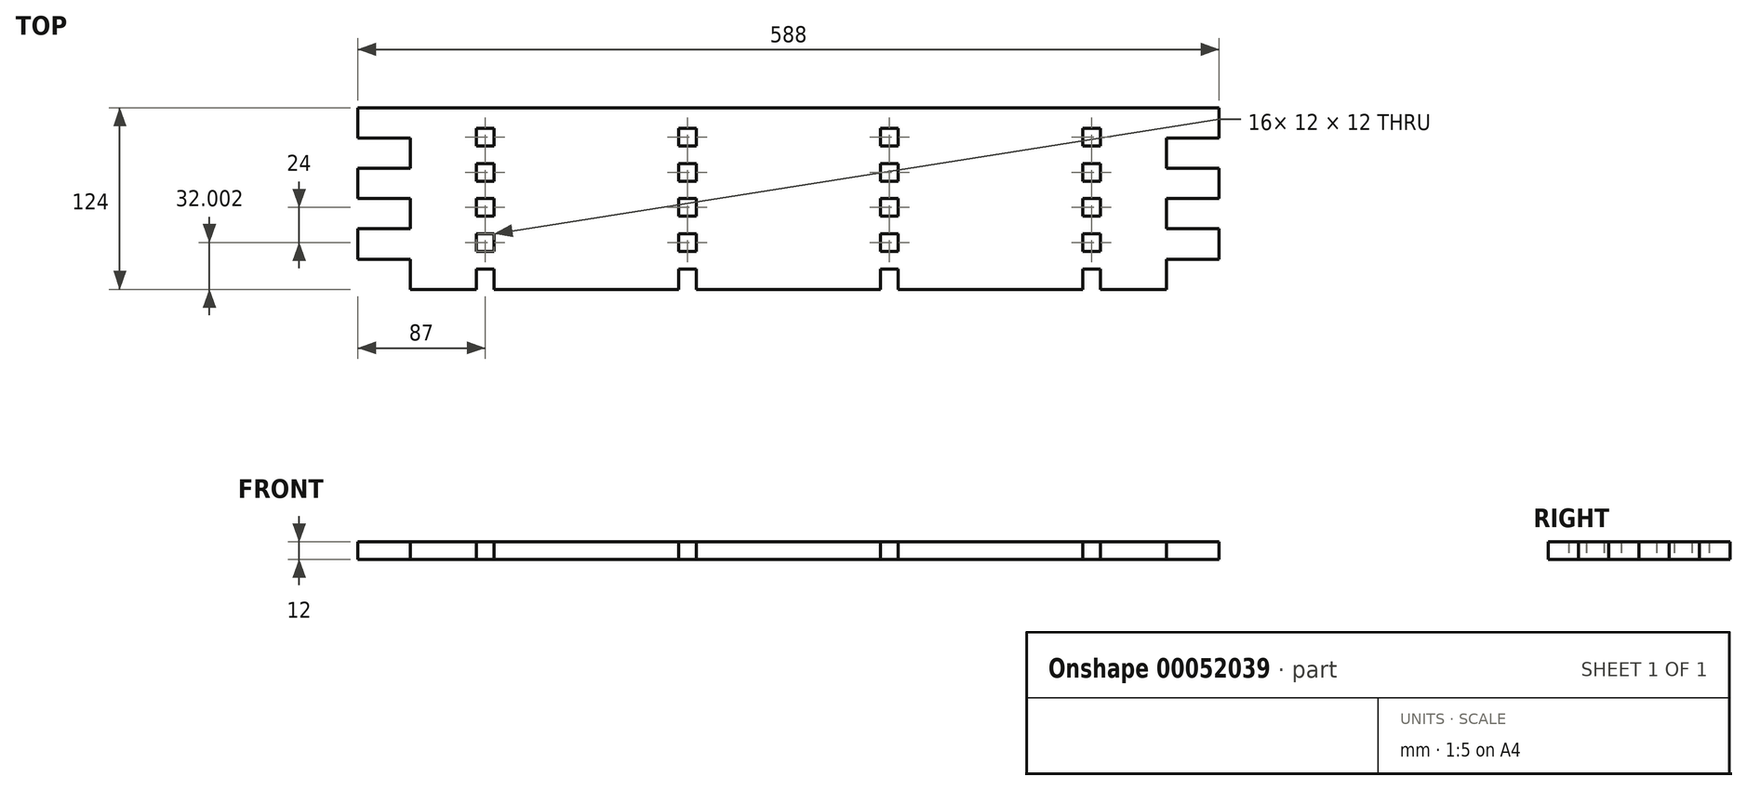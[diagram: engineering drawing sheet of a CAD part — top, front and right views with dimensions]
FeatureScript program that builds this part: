
annotation { "Feature Type Name" : "Feature", "Feature Type Description" : "" }
export const myFeature = defineFeature(function(context is Context, id is Id, definition is map)
    precondition{}
    {
        {
            var Q0;
            Q0=qCreatedBy(makeId("Top.planeOp"),FACE);
            var sketch = newSketch(context, id + "F0", { "sketchPlane" : qUnion([Q0])});
            skLineSegment(sketch, "E0.rect.bottom", {"start": v(489, 62) * mm, "end": v(-489, 62) * mm, "construction": true});
            skLineSegment(sketch, "E0.rect.top", {"start": v(489, -62) * mm, "end": v(-489, -62) * mm, "construction": true});
            skLineSegment(sketch, "E0.rect.left", {"start": v(489, 62) * mm, "end": v(489, -62) * mm, "construction": true});
            skLineSegment(sketch, "E0.rect.right", {"start": v(-489, 62) * mm, "end": v(-489, -62) * mm, "construction": true});
            skPoint(sketch, "E0.rect.middle", {"position": v(0, 0) * mm});
            skLineSegment(sketch, "E1", {"start": v(-489, 120.38) * mm, "end": v(-477, 120.38) * mm, "construction": true});
            skLineSegment(sketch, "E2", {"start": v(-477, 120.38) * mm, "end": v(-351, 120.38) * mm, "construction": true});
            skLineSegment(sketch, "E3.1.0.0", {"start": v(-351, 120.38) * mm, "end": v(-339, 120.38) * mm, "construction": true});
            skLineSegment(sketch, "E3.1.0.1", {"start": v(-339, 120.38) * mm, "end": v(-213, 120.38) * mm, "construction": true});
            skLineSegment(sketch, "E3.2.0.0", {"start": v(-213, 120.38) * mm, "end": v(-201, 120.38) * mm, "construction": true});
            skLineSegment(sketch, "E3.2.0.1", {"start": v(-201, 120.38) * mm, "end": v(-75, 120.38) * mm, "construction": true});
            skLineSegment(sketch, "E3.3.0.0", {"start": v(-75, 120.38) * mm, "end": v(-63, 120.38) * mm, "construction": true});
            skLineSegment(sketch, "E3.3.0.1", {"start": v(-63, 120.38) * mm, "end": v(63, 120.38) * mm, "construction": true});
            skLineSegment(sketch, "E3.4.0.0", {"start": v(63, 120.38) * mm, "end": v(75, 120.38) * mm, "construction": true});
            skLineSegment(sketch, "E3.4.0.1", {"start": v(75, 120.38) * mm, "end": v(201, 120.38) * mm, "construction": true});
            skLineSegment(sketch, "E3.5.0.0", {"start": v(201, 120.38) * mm, "end": v(213, 120.38) * mm, "construction": true});
            skLineSegment(sketch, "E3.5.0.1", {"start": v(213, 120.38) * mm, "end": v(339, 120.38) * mm, "construction": true});
            skLineSegment(sketch, "E3.6.0.0", {"start": v(339, 120.38) * mm, "end": v(351, 120.38) * mm, "construction": true});
            skLineSegment(sketch, "E3.6.0.1", {"start": v(351, 120.38) * mm, "end": v(477, 120.38) * mm, "construction": true});
            skLineSegment(sketch, "E3.direction1", {"start": v(-489, 120.38) * mm, "end": v(-351, 120.38) * mm, "construction": true});
            skLineSegment(sketch, "E4", {"start": v(477, 120.38) * mm, "end": v(489, 120.38) * mm, "construction": true});
            skLineSegment(sketch, "E5", {"start": v(-294, 207.07) * mm, "end": v(-213, 207.07) * mm, "construction": true});
            skPoint(sketch, "E6", {"position": v(0, 207.07) * mm});
            skLineSegment(sketch, "E7", {"start": v(258, 476.96) * mm, "end": v(489, 476.96) * mm, "construction": true});
            skLineSegment(sketch, "E8", {"start": v(294, 207.07) * mm, "end": v(294, 331.07) * mm, "construction": true});
            skLineSegment(sketch, "E9", {"start": v(294, 331.07) * mm, "end": v(-294, 331.07) * mm, "construction": true});
            skLineSegment(sketch, "E10", {"start": v(-294, 331.07) * mm, "end": v(-294, 207.07) * mm, "construction": true});
            skLineSegment(sketch, "E11", {"start": v(258, 289.74) * mm, "end": v(294, 289.74) * mm});
            skLineSegment(sketch, "E12", {"start": v(294, 289.74) * mm, "end": v(294, 269.07) * mm});
            skLineSegment(sketch, "E13", {"start": v(294, 269.07) * mm, "end": v(258, 269.07) * mm});
            skLineSegment(sketch, "E14", {"start": v(258, 269.07) * mm, "end": v(258, 248.4) * mm});
            skLineSegment(sketch, "E15", {"start": v(258, 248.4) * mm, "end": v(294, 248.4) * mm});
            skLineSegment(sketch, "E16", {"start": v(294, 248.4) * mm, "end": v(294, 227.74) * mm});
            skLineSegment(sketch, "E17", {"start": v(294, 227.74) * mm, "end": v(258, 227.74) * mm});
            skLineSegment(sketch, "E18", {"start": v(258, 227.74) * mm, "end": v(258, 207.07) * mm});
            skLineSegment(sketch, "E19", {"start": v(258, 289.74) * mm, "end": v(258, 310.4) * mm});
            skLineSegment(sketch, "E20", {"start": v(258, 310.4) * mm, "end": v(294, 310.4) * mm});
            skLineSegment(sketch, "E21", {"start": v(294, 310.4) * mm, "end": v(294, 331.07) * mm});
            skLineSegment(sketch, "E22", {"start": v(0, 207.07) * mm, "end": v(63, 207.07) * mm});
            skLineSegment(sketch, "E23", {"start": v(0, 331.07) * mm, "end": v(294, 331.07) * mm});
            skLineSegment(sketch, "E24", {"start": v(0, 331.07) * mm, "end": v(0, 207.07) * mm, "construction": true});
            skLineSegment(sketch, "E25.MirrorCS", {"start": v(0, 331.07) * mm, "end": v(-294, 331.07) * mm});
            skLineSegment(sketch, "E26.MirrorCS", {"start": v(0, 207.07) * mm, "end": v(-63, 207.07) * mm});
            skLineSegment(sketch, "E27.MirrorCS", {"start": v(-294, 227.74) * mm, "end": v(-258, 227.74) * mm});
            skLineSegment(sketch, "E28.MirrorCS", {"start": v(-258, 310.4) * mm, "end": v(-294, 310.4) * mm});
            skLineSegment(sketch, "E29.MirrorCS", {"start": v(-294, 269.07) * mm, "end": v(-258, 269.07) * mm});
            skLineSegment(sketch, "E30.MirrorCS", {"start": v(-258, 289.74) * mm, "end": v(-294, 289.74) * mm});
            skLineSegment(sketch, "E31.MirrorCS", {"start": v(-258, 248.4) * mm, "end": v(-294, 248.4) * mm});
            skLineSegment(sketch, "E32.MirrorCS", {"start": v(-258, 227.74) * mm, "end": v(-258, 207.07) * mm});
            skLineSegment(sketch, "E33.MirrorCS", {"start": v(-258, 269.07) * mm, "end": v(-258, 248.4) * mm});
            skLineSegment(sketch, "E34.MirrorCS", {"start": v(-258, 289.74) * mm, "end": v(-258, 310.4) * mm});
            skLineSegment(sketch, "E35.MirrorCS", {"start": v(-294, 207.07) * mm, "end": v(-294, 331.07) * mm, "construction": true});
            skLineSegment(sketch, "E36", {"start": v(-294, 331.07) * mm, "end": v(-294, 310.4) * mm});
            skLineSegment(sketch, "E37", {"start": v(-294, 289.74) * mm, "end": v(-294, 269.07) * mm});
            skLineSegment(sketch, "E38", {"start": v(-294, 227.74) * mm, "end": v(-294, 248.4) * mm, "construction": true});
            skLineSegment(sketch, "E39", {"start": v(-294, 227.74) * mm, "end": v(-294, 248.4) * mm});
            skPoint(sketch, "E40", {"position": v(276, 227.74) * mm});
            skPoint(sketch, "E41", {"position": v(276, 120.38) * mm});
            skLineSegment(sketch, "E42", {"start": v(-213, 207.07) * mm, "end": v(-213, 331.07) * mm, "construction": true});
            skLineSegment(sketch, "E43", {"start": v(-201, 331.07) * mm, "end": v(-201, 207.07) * mm, "construction": true});
            skLineSegment(sketch, "E44", {"start": v(-213, 207.07) * mm, "end": v(-213, 221.07) * mm});
            skLineSegment(sketch, "E45", {"start": v(-213, 221.07) * mm, "end": v(-201, 221.07) * mm});
            skLineSegment(sketch, "E46", {"start": v(-201, 221.07) * mm, "end": v(-201, 207.07) * mm});
            skLineSegment(sketch, "E47", {"start": v(-213, 233.07) * mm, "end": v(-201, 233.07) * mm});
            skLineSegment(sketch, "E48", {"start": v(-201, 233.07) * mm, "end": v(-201, 245.07) * mm});
            skLineSegment(sketch, "E49", {"start": v(-201, 245.07) * mm, "end": v(-213, 245.07) * mm});
            skLineSegment(sketch, "E50", {"start": v(-213, 245.07) * mm, "end": v(-213, 233.07) * mm});
            skLineSegment(sketch, "E51", {"start": v(-294, 269.07) * mm, "end": v(0, 269.07) * mm, "construction": true});
            skLineSegment(sketch, "E52", {"start": v(-213, 257.07) * mm, "end": v(-213, 269.07) * mm});
            skLineSegment(sketch, "E53", {"start": v(-213, 269.07) * mm, "end": v(-201, 269.07) * mm});
            skLineSegment(sketch, "E54", {"start": v(-201, 269.07) * mm, "end": v(-201, 257.07) * mm});
            skLineSegment(sketch, "E55", {"start": v(-213, 257.07) * mm, "end": v(-201, 257.07) * mm});
            skLineSegment(sketch, "E56.trimOffspring", {"start": v(-201, 207.07) * mm, "end": v(-75, 207.07) * mm, "construction": true});
            skLineSegment(sketch, "E57.trimOffspring", {"start": v(-213, 207.07) * mm, "end": v(-258, 207.07) * mm});
            skLineSegment(sketch, "E58", {"start": v(-213, 269.07) * mm, "end": v(-213, 281.07) * mm, "construction": true});
            skLineSegment(sketch, "E59", {"start": v(-213, 281.07) * mm, "end": v(-213, 293.07) * mm, "construction": true});
            skLineSegment(sketch, "E60", {"start": v(-213, 293.07) * mm, "end": v(-213, 305.07) * mm, "construction": true});
            skLineSegment(sketch, "E61", {"start": v(-213, 305.07) * mm, "end": v(-213, 317.07) * mm, "construction": true});
            skLineSegment(sketch, "E62", {"start": v(-213, 281.07) * mm, "end": v(-201, 281.07) * mm});
            skLineSegment(sketch, "E63", {"start": v(-213, 293.07) * mm, "end": v(-201, 293.07) * mm});
            skLineSegment(sketch, "E64", {"start": v(-213, 317.07) * mm, "end": v(-201, 317.07) * mm});
            skLineSegment(sketch, "E65", {"start": v(-213, 305.07) * mm, "end": v(-201, 305.07) * mm});
            skLineSegment(sketch, "E66", {"start": v(-213, 293.07) * mm, "end": v(-213, 281.07) * mm});
            skLineSegment(sketch, "E67", {"start": v(-201, 293.07) * mm, "end": v(-201, 281.07) * mm});
            skLineSegment(sketch, "E68", {"start": v(-201, 305.07) * mm, "end": v(-201, 317.07) * mm});
            skLineSegment(sketch, "E69", {"start": v(-213, 317.07) * mm, "end": v(-213, 305.07) * mm});
            skLineSegment(sketch, "E70", {"start": v(-213, 207.07) * mm, "end": v(-201, 207.07) * mm, "construction": true});
            skLineSegment(sketch, "E71.1.0.0", {"start": v(-163, 221.07) * mm, "end": v(-151, 221.07) * mm});
            skLineSegment(sketch, "E71.2.0.0", {"start": v(-113, 221.07) * mm, "end": v(-101, 221.07) * mm});
            skLineSegment(sketch, "E71.direction1", {"start": v(-213, 221.07) * mm, "end": v(-163, 221.07) * mm, "construction": true});
            skLineSegment(sketch, "E72.1.0.0", {"start": v(-75, 269.07) * mm, "end": v(-63, 269.07) * mm});
            skLineSegment(sketch, "E72.1.0.1", {"start": v(-63, 221.07) * mm, "end": v(-63, 207.07) * mm});
            skLineSegment(sketch, "E72.1.0.2", {"start": v(-75, 269.07) * mm, "end": v(-75, 281.07) * mm, "construction": true});
            skLineSegment(sketch, "E72.1.0.3", {"start": v(-75, 293.07) * mm, "end": v(-75, 305.07) * mm, "construction": true});
            skLineSegment(sketch, "E72.1.0.4", {"start": v(-75, 293.07) * mm, "end": v(-63, 293.07) * mm});
            skLineSegment(sketch, "E72.1.0.5", {"start": v(-63, 305.07) * mm, "end": v(-63, 317.07) * mm});
            skLineSegment(sketch, "E72.1.0.6", {"start": v(-75, 207.07) * mm, "end": v(-75, 331.07) * mm, "construction": true});
            skLineSegment(sketch, "E72.1.0.7", {"start": v(-63, 293.07) * mm, "end": v(-63, 281.07) * mm});
            skLineSegment(sketch, "E72.1.0.9", {"start": v(-75, 245.07) * mm, "end": v(-75, 233.07) * mm});
            skLineSegment(sketch, "E72.1.0.10", {"start": v(-75, 317.07) * mm, "end": v(-75, 305.07) * mm});
            skLineSegment(sketch, "E72.1.0.11", {"start": v(-63, 331.07) * mm, "end": v(-63, 207.07) * mm, "construction": true});
            skLineSegment(sketch, "E72.1.0.12", {"start": v(-75, 207.07) * mm, "end": v(-75, 221.07) * mm});
            skLineSegment(sketch, "E72.1.0.13", {"start": v(-63, 269.07) * mm, "end": v(-63, 257.07) * mm});
            skLineSegment(sketch, "E72.1.0.14", {"start": v(-75, 293.07) * mm, "end": v(-75, 281.07) * mm});
            skLineSegment(sketch, "E72.1.0.15", {"start": v(-75, 257.07) * mm, "end": v(-75, 269.07) * mm});
            skLineSegment(sketch, "E72.1.0.16", {"start": v(-63, 233.07) * mm, "end": v(-63, 245.07) * mm});
            skLineSegment(sketch, "E72.1.0.17", {"start": v(-75, 221.07) * mm, "end": v(-63, 221.07) * mm});
            skLineSegment(sketch, "E72.1.0.18", {"start": v(-75, 305.07) * mm, "end": v(-75, 317.07) * mm, "construction": true});
            skLineSegment(sketch, "E72.1.0.19", {"start": v(-63, 245.07) * mm, "end": v(-75, 245.07) * mm});
            skLineSegment(sketch, "E72.1.0.20", {"start": v(-75, 317.07) * mm, "end": v(-63, 317.07) * mm});
            skLineSegment(sketch, "E72.1.0.21", {"start": v(-75, 281.07) * mm, "end": v(-75, 293.07) * mm, "construction": true});
            skLineSegment(sketch, "E72.1.0.22", {"start": v(-75, 257.07) * mm, "end": v(-63, 257.07) * mm});
            skLineSegment(sketch, "E72.1.0.23", {"start": v(-75, 305.07) * mm, "end": v(-63, 305.07) * mm});
            skLineSegment(sketch, "E72.1.0.24", {"start": v(-75, 233.07) * mm, "end": v(-63, 233.07) * mm});
            skLineSegment(sketch, "E72.1.0.25", {"start": v(-75, 281.07) * mm, "end": v(-63, 281.07) * mm});
            skLineSegment(sketch, "E72.2.0.0", {"start": v(63, 269.07) * mm, "end": v(75, 269.07) * mm});
            skLineSegment(sketch, "E72.2.0.1", {"start": v(75, 221.07) * mm, "end": v(75, 207.07) * mm});
            skLineSegment(sketch, "E72.2.0.2", {"start": v(63, 269.07) * mm, "end": v(63, 281.07) * mm, "construction": true});
            skLineSegment(sketch, "E72.2.0.3", {"start": v(63, 293.07) * mm, "end": v(63, 305.07) * mm, "construction": true});
            skLineSegment(sketch, "E72.2.0.4", {"start": v(63, 293.07) * mm, "end": v(75, 293.07) * mm});
            skLineSegment(sketch, "E72.2.0.5", {"start": v(75, 305.07) * mm, "end": v(75, 317.07) * mm});
            skLineSegment(sketch, "E72.2.0.6", {"start": v(63, 207.07) * mm, "end": v(63, 331.07) * mm, "construction": true});
            skLineSegment(sketch, "E72.2.0.7", {"start": v(75, 293.07) * mm, "end": v(75, 281.07) * mm});
            skLineSegment(sketch, "E72.2.0.9", {"start": v(63, 245.07) * mm, "end": v(63, 233.07) * mm});
            skLineSegment(sketch, "E72.2.0.10", {"start": v(63, 317.07) * mm, "end": v(63, 305.07) * mm});
            skLineSegment(sketch, "E72.2.0.11", {"start": v(75, 331.07) * mm, "end": v(75, 207.07) * mm, "construction": true});
            skLineSegment(sketch, "E72.2.0.12", {"start": v(63, 207.07) * mm, "end": v(63, 221.07) * mm});
            skLineSegment(sketch, "E72.2.0.13", {"start": v(75, 269.07) * mm, "end": v(75, 257.07) * mm});
            skLineSegment(sketch, "E72.2.0.14", {"start": v(63, 293.07) * mm, "end": v(63, 281.07) * mm});
            skLineSegment(sketch, "E72.2.0.15", {"start": v(63, 257.07) * mm, "end": v(63, 269.07) * mm});
            skLineSegment(sketch, "E72.2.0.16", {"start": v(75, 233.07) * mm, "end": v(75, 245.07) * mm});
            skLineSegment(sketch, "E72.2.0.17", {"start": v(63, 221.07) * mm, "end": v(75, 221.07) * mm});
            skLineSegment(sketch, "E72.2.0.18", {"start": v(63, 305.07) * mm, "end": v(63, 317.07) * mm, "construction": true});
            skLineSegment(sketch, "E72.2.0.19", {"start": v(75, 245.07) * mm, "end": v(63, 245.07) * mm});
            skLineSegment(sketch, "E72.2.0.20", {"start": v(63, 317.07) * mm, "end": v(75, 317.07) * mm});
            skLineSegment(sketch, "E72.2.0.21", {"start": v(63, 281.07) * mm, "end": v(63, 293.07) * mm, "construction": true});
            skLineSegment(sketch, "E72.2.0.22", {"start": v(63, 257.07) * mm, "end": v(75, 257.07) * mm});
            skLineSegment(sketch, "E72.2.0.23", {"start": v(63, 305.07) * mm, "end": v(75, 305.07) * mm});
            skLineSegment(sketch, "E72.2.0.24", {"start": v(63, 233.07) * mm, "end": v(75, 233.07) * mm});
            skLineSegment(sketch, "E72.2.0.25", {"start": v(63, 281.07) * mm, "end": v(75, 281.07) * mm});
            skLineSegment(sketch, "E72.direction1", {"start": v(-213, 207.07) * mm, "end": v(-75, 207.07) * mm, "construction": true});
            skLineSegment(sketch, "E73.0.3.0", {"start": v(201, 269.07) * mm, "end": v(213, 269.07) * mm});
            skLineSegment(sketch, "E73.3.3.0", {"start": v(213, 221.07) * mm, "end": v(213, 207.07) * mm});
            skLineSegment(sketch, "E73.6.3.0", {"start": v(201, 269.07) * mm, "end": v(201, 281.07) * mm, "construction": true});
            skLineSegment(sketch, "E73.9.3.0", {"start": v(201, 293.07) * mm, "end": v(201, 305.07) * mm, "construction": true});
            skLineSegment(sketch, "E73.12.3.0", {"start": v(201, 293.07) * mm, "end": v(213, 293.07) * mm});
            skLineSegment(sketch, "E73.15.3.0", {"start": v(213, 305.07) * mm, "end": v(213, 317.07) * mm});
            skLineSegment(sketch, "E73.18.3.0", {"start": v(201, 207.07) * mm, "end": v(201, 331.07) * mm, "construction": true});
            skLineSegment(sketch, "E73.21.3.0", {"start": v(213, 293.07) * mm, "end": v(213, 281.07) * mm});
            skLineSegment(sketch, "E73.27.3.0", {"start": v(201, 245.07) * mm, "end": v(201, 233.07) * mm});
            skLineSegment(sketch, "E73.30.3.0", {"start": v(201, 317.07) * mm, "end": v(201, 305.07) * mm});
            skLineSegment(sketch, "E73.33.3.0", {"start": v(213, 331.07) * mm, "end": v(213, 207.07) * mm, "construction": true});
            skLineSegment(sketch, "E73.36.3.0", {"start": v(201, 207.07) * mm, "end": v(201, 221.07) * mm});
            skLineSegment(sketch, "E73.39.3.0", {"start": v(213, 269.07) * mm, "end": v(213, 257.07) * mm});
            skLineSegment(sketch, "E73.42.3.0", {"start": v(201, 293.07) * mm, "end": v(201, 281.07) * mm});
            skLineSegment(sketch, "E73.45.3.0", {"start": v(201, 257.07) * mm, "end": v(201, 269.07) * mm});
            skLineSegment(sketch, "E73.48.3.0", {"start": v(213, 233.07) * mm, "end": v(213, 245.07) * mm});
            skLineSegment(sketch, "E73.51.3.0", {"start": v(201, 221.07) * mm, "end": v(213, 221.07) * mm});
            skLineSegment(sketch, "E73.54.3.0", {"start": v(201, 305.07) * mm, "end": v(201, 317.07) * mm, "construction": true});
            skLineSegment(sketch, "E73.57.3.0", {"start": v(213, 245.07) * mm, "end": v(201, 245.07) * mm});
            skLineSegment(sketch, "E73.60.3.0", {"start": v(201, 317.07) * mm, "end": v(213, 317.07) * mm});
            skLineSegment(sketch, "E73.63.3.0", {"start": v(201, 281.07) * mm, "end": v(201, 293.07) * mm, "construction": true});
            skLineSegment(sketch, "E73.66.3.0", {"start": v(201, 257.07) * mm, "end": v(213, 257.07) * mm});
            skLineSegment(sketch, "E73.69.3.0", {"start": v(201, 305.07) * mm, "end": v(213, 305.07) * mm});
            skLineSegment(sketch, "E73.72.3.0", {"start": v(201, 233.07) * mm, "end": v(213, 233.07) * mm});
            skLineSegment(sketch, "E73.75.3.0", {"start": v(201, 281.07) * mm, "end": v(213, 281.07) * mm});
            skLineSegment(sketch, "E74.trimOffspring", {"start": v(75, 207.07) * mm, "end": v(201, 207.07) * mm, "construction": true});
            skLineSegment(sketch, "E75.trimOffspring", {"start": v(213, 207.07) * mm, "end": v(294, 207.07) * mm, "construction": true});
            skLineSegment(sketch, "E76.trimOffspring", {"start": v(213, 207.07) * mm, "end": v(258, 207.07) * mm});
            skLineSegment(sketch, "E77.trimOffspring", {"start": v(75, 207.07) * mm, "end": v(201, 207.07) * mm});
            skLineSegment(sketch, "E78.trimOffspring", {"start": v(-63, 207.07) * mm, "end": v(0, 207.07) * mm, "construction": true});
            skLineSegment(sketch, "E79.trimOffspring", {"start": v(-75, 207.07) * mm, "end": v(-201, 207.07) * mm});
            skSolve(sketch);
        }
        {
            var Q0;
            Q0=qSketchRegion(id+"F0",true);
            extrude(context, id + "F1", {"entities" : qUnion([Q0]), "depth" : 12 * mm});
        }
    });
